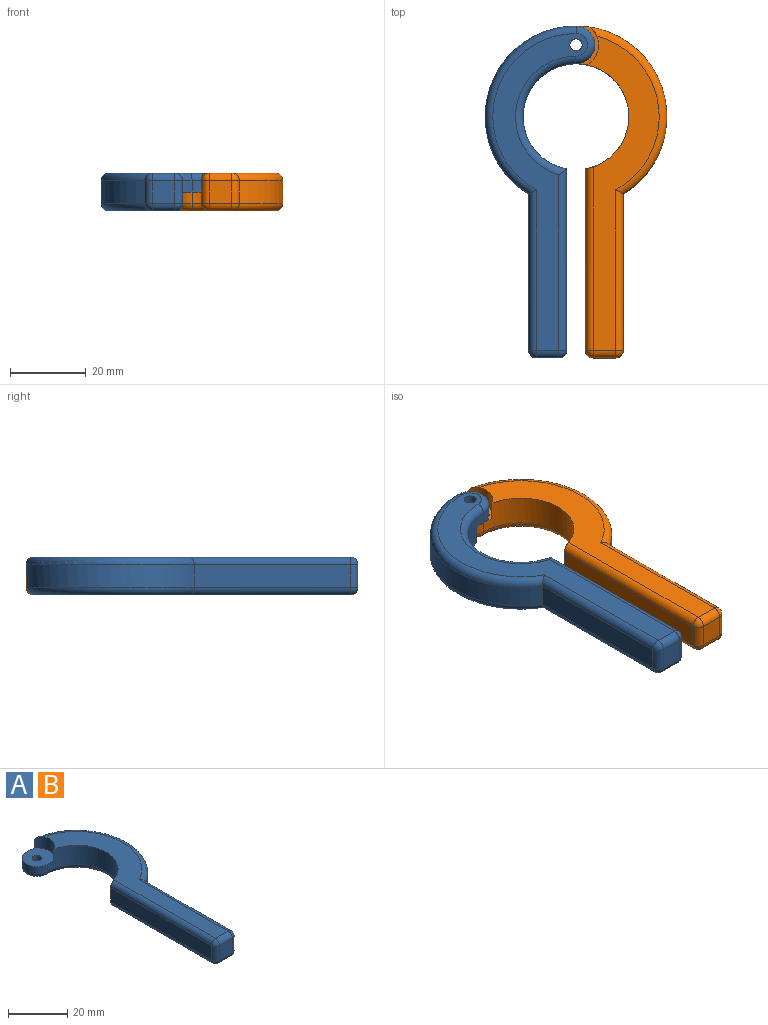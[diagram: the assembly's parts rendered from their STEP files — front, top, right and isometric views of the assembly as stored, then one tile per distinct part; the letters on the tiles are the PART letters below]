
ASSEMBLY  parts=2 mates=1
PART A: 27 faces, bbox 31.4x89.8x10 mm
  f0: cylinder r=14mm len=27.78mm, axis (0,0,1), area 316.6mm2, adj f3,f5,f7,f8,f9,f14,f26
  f1: cylinder r=24mm len=44.49mm, axis (0,0,1), area 362.3mm2, adj f4,f7,f8,f9,f11,f23
  f2: plane 6x6mm, normal (0,-1,0), area 36mm2, adj f15,f16,f19,f20
  f3: plane 48x6mm, normal (-1,0,0), area 288mm2, adj f0,f14,f19,f24
  f4: plane 41.29x6mm, normal (1,0,0), area 247.7mm2, adj f1,f12,f16,f21
  f5: plane 83.06x19.17mm, normal (0,0,1), area 620.6mm2, adj f0,f9,f11,f12,f14,f15
  f6: plane 83.78x25mm, normal (0,0,-1), area 584mm2, adj f10,f20,f21,f23,f24,f25,f26
  f7: plane 11x10.29mm, normal (0,0,1), area 83.3mm2, adj f0,f1,f8,f9,f10
  f8: cylinder r=5mm len=10mm, axis (0,0,-1), area 47.1mm2, adj f0,f1,f7,f25
  f9: cylinder r=6mm len=10mm, axis (0,0,-1), area 58mm2, adj f0,f1,f5,f7,f11
  f10: cylinder r=1.6mm len=5mm, axis (0,0,-1), area 50.3mm2, adj f6,f7
  f11: torus R=22mm, axis (0,0,1), area 176.6mm2, adj f1,f5,f9,f12
  f12: cylinder r=2mm len=42.44mm, axis (0,1,0), area 131mm2, adj f4,f5,f11,f13
  f13: sphere r=2mm, area 6.3mm2, adj f12,f15,f16
  f14: cylinder r=2mm len=48.52mm, axis (0,1,0), area 151.3mm2, adj f0,f3,f5,f17
  f15: cylinder r=2mm len=6mm, axis (1,0,0), area 18.8mm2, adj f2,f5,f13,f17
  f16: cylinder r=2mm len=6mm, axis (0,0,-1), area 18.8mm2, adj f2,f4,f13,f18
  f17: sphere r=2mm, area 6.3mm2, adj f14,f15,f19
  f18: sphere r=2mm, area 6.3mm2, adj f16,f20,f21
  f19: cylinder r=2mm len=6mm, axis (0,0,1), area 18.8mm2, adj f2,f3,f17,f22
  f20: cylinder r=2mm len=6mm, axis (-1,0,0), area 18.8mm2, adj f2,f6,f18,f22
  f21: cylinder r=2mm len=42.44mm, axis (0,1,0), area 131mm2, adj f4,f6,f18,f23
  f22: sphere r=2mm, area 6.3mm2, adj f19,f20,f24
  f23: torus R=22mm, axis (0,0,-1), area 190.9mm2, adj f1,f6,f21,f25
  f24: cylinder r=2mm len=48mm, axis (0,1,0), area 149mm2, adj f3,f6,f22,f26
  f25: torus R=3mm, axis (0,0,-1), area 42.2mm2, adj f6,f8,f23,f26
  f26: torus R=16mm, axis (0,0,-1), area 135.1mm2, adj f0,f6,f24,f25
PART B: same geometry as A
PLACE A rot(axis=(0,1,0),180deg) t=(-14.48,14.25,0.85)mm
PLACE B t=(-14.48,14.25,-9.15)mm
MATE revolute A.f8 <-> B.f8  axis (0,0,-1) through (-14.48,33.25,-4.15)mm
